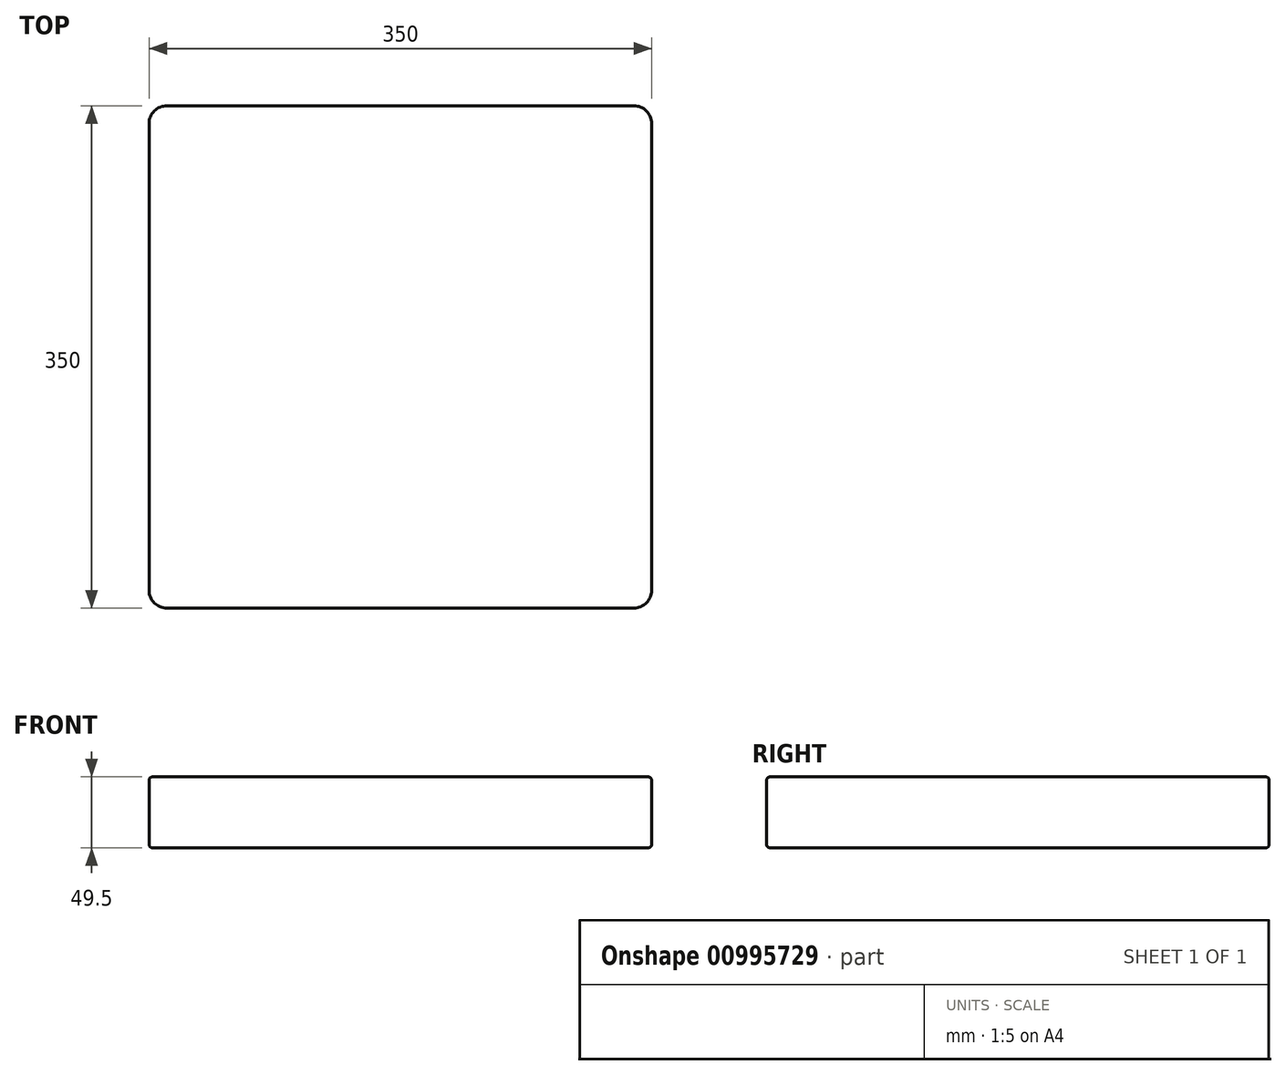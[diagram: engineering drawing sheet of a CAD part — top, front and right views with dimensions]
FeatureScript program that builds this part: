
annotation { "Feature Type Name" : "Feature", "Feature Type Description" : "" }
export const myFeature = defineFeature(function(context is Context, id is Id, definition is map)
    precondition{}
    {
        {
            var Q0;
            Q0=qCreatedBy(makeId("Top.planeOp"),FACE);
            var sketch = newSketch(context, id + "F0", { "sketchPlane" : qUnion([Q0])});
            skLineSegment(sketch, "E0.bottom", {"start": v(175, -175) * mm, "end": v(-175, -175) * mm});
            skLineSegment(sketch, "E0.top", {"start": v(175, 175) * mm, "end": v(-175, 175) * mm});
            skLineSegment(sketch, "E0.left", {"start": v(175, -175) * mm, "end": v(175, 175) * mm});
            skLineSegment(sketch, "E0.right", {"start": v(-175, -175) * mm, "end": v(-175, 175) * mm});
            skPoint(sketch, "E0.middle", {"position": v(0, 0) * mm});
            skSolve(sketch);
        }
        {
            var Q0;
            Q0=makeQuery(id+"F0.imprint","IMPRINT",FACE,{"disambiguationData":[TD([[makeQuery(id+"F0.imprint","IMPRINT",EDGE,{"derivedFrom":sQuery(id+"F0.wireOp",EDGE,"E0.bottom")}),-1.0]])]});
            extrude(context, id + "F1", {"entities" : qUnion([Q0]), "depth" : 49.5 * mm, "offsetDistance" : 25.4 * mm});
        }
        {
            var Q0;
            Q0=makeQuery(id+"F1.opExtrude","SWEPT_EDGE",EDGE,{"disambiguationData":[OSD([sQuery(id+"F0.wireOp",EDGE,"E0.bottom"),sQuery(id+"F0.wireOp",EDGE,"E0.left")])]});
            var Q1;
            Q1=makeQuery(id+"F1.opExtrude","SWEPT_EDGE",EDGE,{"disambiguationData":[OSD([sQuery(id+"F0.wireOp",EDGE,"E0.top"),sQuery(id+"F0.wireOp",EDGE,"E0.left")])]});
            var Q2;
            Q2=makeQuery(id+"F1.opExtrude","SWEPT_EDGE",EDGE,{"disambiguationData":[OSD([sQuery(id+"F0.wireOp",EDGE,"E0.top"),sQuery(id+"F0.wireOp",EDGE,"E0.right")])]});
            var Q3;
            Q3=makeQuery(id+"F1.opExtrude","SWEPT_EDGE",EDGE,{"disambiguationData":[OSD([sQuery(id+"F0.wireOp",EDGE,"E0.bottom"),sQuery(id+"F0.wireOp",EDGE,"E0.right")])]});
            fillet(context, id + "F2", {"entities" : qUnion([Q0, Q1, Q2, Q3]), "radius" : 12.5 * mm, "tangentPropagation" : true, "allowEdgeOverflow" : false});
        }
        {
            var Q0;
            Q0=makeQuery(id+"F1.opExtrude","CAP_EDGE",EDGE,{"disambiguationData":[OSD([sQuery(id+"F0.wireOp",EDGE,"E0.bottom")])],"isStart":true});
            var Q1;
            Q1=makeQuery(id+"F1.opExtrude","CAP_EDGE",EDGE,{"disambiguationData":[OSD([sQuery(id+"F0.wireOp",EDGE,"E0.bottom")])],"isStart":false});
            fillet(context, id + "F3", {"entities" : qUnion([Q0, Q1]), "radius" : 2.5 * mm, "tangentPropagation" : true, "allowEdgeOverflow" : false});
        }
    });
